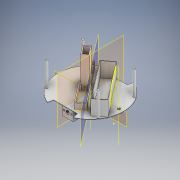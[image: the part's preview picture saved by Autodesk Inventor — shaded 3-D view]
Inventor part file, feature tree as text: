
AUTODESK INVENTOR PART (.ipt)
format: ipt  version: 2020 (Build 240168000, 168)  size: 561,152 bytes
history: native  units: mm
features: sketch x14, other x10, extrude x7, reference x5, plane x3, projected_geometry x3, mirror x2, revolve x1, pattern_circular x1
ambient origin geometry x8: Origin, YZ Plane, XZ Plane, XY Plane, X Axis, Y Axis, Z Axis, Center Point
bodies: Solid1 (feature_tree)
feature tree (46):
  other  "Assembly1.iam"
  other  "KonstrukcijaDonjiDio_v.1.1.ipt:1"
  other  "DropMechanism_v.1.2.ipt:1"
  extrude  "Extrusion1"  Depth=5.0mm
  mirror  "Mirror1"
  plane  "Work Plane3"
  mirror  "Mirror2"
  sketch  "Sketch6"  dims[d43=11.0mm d44=13.0mm]
  sketch  "Sketch7"  dims[d45=4.0mm d46=0.0mm d47=0.5mm]
  extrude  "Extrusion2"  Depth=2.0mm TaperAngle=0.0deg
  extrude  "Extrusion3"  Depth=8.0mm
  extrude  "Extrusion5"  Depth=5.0mm
  sketch  "Sketch11"  dims[d55=1.0mm d56=0.0mm d22=0.5mm]
  sketch  "Sketch12"  dims[d23=0.872665mm]
  other  "Work Axis2"
  extrude  "Extrusion9"  Depth=13.0mm
  sketch  "Sketch18"  dims[d25=0.872665mm]
  other  "Work Axis3"
  revolve  "Revolution1"  [1 undecoded]
  pattern_circular  "Circular Pattern4"  Count=20 Angle=360.0deg
  extrude  "Extrusion10"  Depth=1.0mm TaperAngle=0.0deg
  extrude  "Extrusion11"  Depth=0.5mm
  plane  "Work Plane1"
  sketch  "Sketch2"  dims[d0=10.0mm d1=5.0mm]
  plane  "Work Plane1_1"
  sketch  "Sketch3"  dims[d2=55.0mm d3=0.0mm d4=2.0mm d5=0.0mm]
  sketch  "Sketch4"  dims[d6=2.0mm d7=0.0mm d11=8.0mm]
  other  "Srf1"
  sketch  "Sketch5"  dims[d12=1.0mm d13=0.0mm d42=5.0mm]
  projected_geometry  "Projected Loop1"
  projected_geometry  "Projected Loop2"
  sketch  "Sketch8"  dims[d48=2.164208mm d49=200.0mm d50=360.0deg]
  projected_geometry  "Projected Loop3"
  sketch  "Sketch10"  dims[d52=6.0mm d53=1.0mm d54=0.0mm]
  reference  "Reference1"
  reference  "Reference2"
  reference  "Reference3"
  reference  "Reference4"
  reference  "Reference5"
  sketch  "Sketch17"  dims[d24=0.5mm]
  sketch  "Sketch19"
  sketch  "Sketch20"
  other  "Srf1::Derived"
  other  "<userpath>\Documents\Draws_Inventor\Inventor_Robocup\Robot_assembly.iam"
  other  "Robot_assembly.iam"
  other  "Extension board:1"
note: 1 required parameter value undecoded (feature->parameter linkage not recoverable at this tier; creation-order binding heuristic only, values carry confidence <= 0.55)
